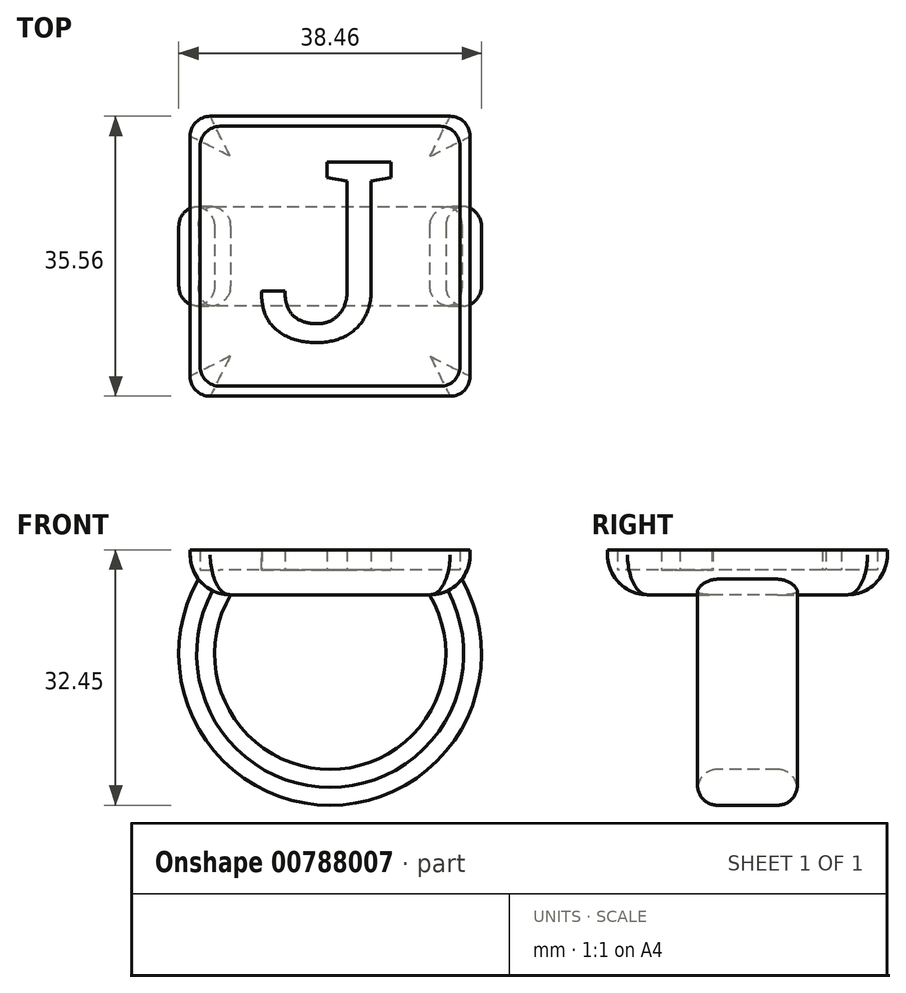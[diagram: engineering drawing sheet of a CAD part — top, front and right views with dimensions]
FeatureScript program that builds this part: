
annotation { "Feature Type Name" : "Feature", "Feature Type Description" : "" }
export const myFeature = defineFeature(function(context is Context, id is Id, definition is map)
    precondition{}
    {
        {
            var Q0;
            Q0=qCreatedBy(makeId("Top.planeOp"),FACE);
            var sketch = newSketch(context, id + "F0", { "sketchPlane" : qUnion([Q0])});
            skLineSegment(sketch, "E0.bottom", {"start": v(17.78, -17.78) * mm, "end": v(-17.78, -17.78) * mm});
            skLineSegment(sketch, "E0.top", {"start": v(17.78, 17.78) * mm, "end": v(-17.78, 17.78) * mm});
            skLineSegment(sketch, "E0.left", {"start": v(17.78, -17.78) * mm, "end": v(17.78, 17.78) * mm});
            skLineSegment(sketch, "E0.right", {"start": v(-17.78, -17.78) * mm, "end": v(-17.78, 17.78) * mm});
            skPoint(sketch, "E0.middle", {"position": v(0, 0) * mm});
            skSolve(sketch);
        }
        {
            var Q0;
            Q0 = qSketchRegion(id + "F0", true);
            extrude(context, id + "F1", {"entities" : qUnion([Q0]), "depth" : 3.17 * mm, "offsetDistance" : 25 * mm});
        }
        {
            var Q0;
            Q0=qCreatedBy(makeId("Front.planeOp"),FACE);
            var sketch = newSketch(context, id + "F2", { "sketchPlane" : qUnion([Q0])});
            skArc(sketch, "E1", {"start": v(-14.7, 0) * mm, "mid": v(0, -24.01) * mm, "end": v(14.7, 0) * mm});
            skSolve(sketch);
        }
        {
            var Q0;
            Q0=makeQuery(id+"F1.opExtrude","CAP_FACE",FACE,{"disambiguationData":[OSD([sQuery(id+"F0.wireOp",EDGE,"E0.bottom"),sQuery(id+"F0.wireOp",EDGE,"E0.top"),sQuery(id+"F0.wireOp",EDGE,"E0.left"),sQuery(id+"F0.wireOp",EDGE,"E0.right")])],"isStart":true});
            var sketch = newSketch(context, id + "F3", { "sketchPlane" : qUnion([Q0])});
            skLineSegment(sketch, "E2.bottom", {"start": v(-12.62, -6.35) * mm, "end": v(-17.7, -6.35) * mm});
            skLineSegment(sketch, "E2.top", {"start": v(-12.62, 6.35) * mm, "end": v(-17.7, 6.35) * mm});
            skLineSegment(sketch, "E2.left", {"start": v(-12.62, -6.35) * mm, "end": v(-12.62, 6.35) * mm});
            skLineSegment(sketch, "E2.right", {"start": v(-17.7, -6.35) * mm, "end": v(-17.7, 6.35) * mm});
            skPoint(sketch, "E2.middle", {"position": v(-15.16, 0) * mm});
            skSolve(sketch);
        }
        {
            var Q0;
            Q0=makeQuery(id+"F3.imprint","IMPRINT",FACE,{"disambiguationData":[TD([[makeQuery(id+"F3.imprint","IMPRINT",EDGE,{"derivedFrom":sQuery(id+"F3.wireOp",EDGE,"E2.bottom")}),-1.0]])]});
            var Q1;
            Q1 = qConstructionFilter(qBodyType(qCreatedBy(id + "F2" ,EDGE), BodyType.WIRE), ConstructionObject.NO);
            sweep(context, id + "F4", {"operationType" : NewBodyOperationType.ADD, "profiles" : qUnion([Q0]), "path" : qUnion([Q1])});
        }
        {
            var Q0;
            Q0=makeQuery(id+"F4.opSweep","SWEPT_FACE",FACE,{"disambiguationData":[OSD([sQuery(id+"F2.wireOp",EDGE,"E1"),sQuery(id+"F3.wireOp",EDGE,"E2.top")])]});
            var sketch = newSketch(context, id + "F5", { "sketchPlane" : qUnion([Q0])});
            skLineSegment(sketch, "E3.0", {"start": v(17.78, 0) * mm, "end": v(-17.78, 0) * mm});
            skArc(sketch, "E3.1", {"start": v(-12.62, 0) * mm, "mid": v(0, -22.19) * mm, "end": v(12.62, 0) * mm});
            skLineSegment(sketch, "E3.2", {"start": v(13.48, -1.69) * mm, "end": v(14.7, 0) * mm});
            skSolve(sketch);
        }
        {
            var Q0;
            {var subQ0=sQuery(id+"F5.wireOp",EDGE,"E3.2");Q0=makeQuery(id+"F5.imprint","IMPRINT",FACE,{"disambiguationData":[TD([[makeQuery(id+"F5.imprint","IMPRINT",EDGE,{"derivedFrom":subQ0}),1.0]])]});}
            var Q1;
            Q1=makeQuery(id+"F4.opSweep","SWEPT_FACE",FACE,{"disambiguationData":[OSD([sQuery(id+"F2.wireOp",EDGE,"E1"),sQuery(id+"F3.wireOp",EDGE,"E2.top")])]});
            var Q2;
            Q2=makeQuery(id+"F4.opSweep","SWEPT_FACE",FACE,{"disambiguationData":[OSD([sQuery(id+"F2.wireOp",EDGE,"E1"),sQuery(id+"F3.wireOp",EDGE,"E2.bottom")])]});
            extrude(context, id + "F6", {"entities" : qUnion([Q0]), "operationType" : NewBodyOperationType.ADD, "depth" : 0 * mm, "endBoundEntityFace" : qUnion([Q1]), "offsetDistance" : 25.4 * mm, "hasSecondDirection" : true, "secondDirectionBound" : SecondDirectionBoundingType.UP_TO_SURFACE, "secondDirectionOppositeDirection" : true, "secondDirectionDepth" : 25.4 * mm, "secondDirectionBoundEntityFace" : qUnion([Q2])});
        }
        {
            var Q0;
            Q0=makeQuery(id+"F6.boolean.opBoolean","MERGE",EDGE,{"derivedFrom":[makeQuery(id+"F4.opSweep","SWEPT_EDGE",EDGE,{"disambiguationData":[OSD([sQuery(id+"F2.wireOp",EDGE,"E1"),sQuery(id+"F3.wireOp",EDGE,"E2.top"),sQuery(id+"F3.wireOp",EDGE,"E2.left")])]}),makeQuery(id+"F6.opExtrude","CAP_EDGE",EDGE,{"disambiguationData":[OSD([sQuery(id+"F5.wireOp",EDGE,"E3.1")])],"isStart":false})]});
            var Q1;
            {var subQ0=sQuery(id+"F5.wireOp",EDGE,"E3.1");var subQ1=sQuery(id+"F3.wireOp",EDGE,"E2.bottom");var subQ2=sQuery(id+"F2.wireOp",EDGE,"E1");Q1=makeQuery(id+"F6.boolean.opBoolean","MERGE",EDGE,{"derivedFrom":[makeQuery(id+"F4.opSweep","SWEPT_EDGE",EDGE,{"disambiguationData":[OSD([subQ2,subQ1,sQuery(id+"F3.wireOp",EDGE,"E2.left")])]}),makeQuery(id+"F6.opExtrude","TWEAK_EDGE",EDGE,{"derivedFrom":[makeQuery(id+"F4.opSweep","SWEPT_FACE",FACE,{"disambiguationData":[OSD([subQ2,subQ1])]}),makeQuery(id+"F5.imprint","IMPRINT",EDGE,{"disambiguationData":[TD([[makeQuery(id+"F5.imprint","INTERSECT",VERTEX,{"derivedFrom":[subQ0,sQuery(id+"F5.wireOp",EDGE,"E3.2")]}),-1.0]])],"derivedFrom":subQ0})]})]});}
            var Q2;
            Q2=makeQuery(id+"F4.opSweep","SWEPT_EDGE",EDGE,{"disambiguationData":[OSD([sQuery(id+"F2.wireOp",EDGE,"E1"),sQuery(id+"F3.wireOp",EDGE,"E2.top"),sQuery(id+"F3.wireOp",EDGE,"E2.right")])]});
            var Q3;
            Q3=makeQuery(id+"F4.opSweep","SWEPT_EDGE",EDGE,{"disambiguationData":[OSD([sQuery(id+"F2.wireOp",EDGE,"E1"),sQuery(id+"F3.wireOp",EDGE,"E2.bottom"),sQuery(id+"F3.wireOp",EDGE,"E2.right")])]});
            fillet(context, id + "F7", {"entities" : qUnion([Q0, Q1, Q2, Q3]), "radius" : 2.54 * mm, "tangentPropagation" : true, "allowEdgeOverflow" : false});
        }
        {
            var Q0;
            Q0=makeQuery(id+"F1.opExtrude","CAP_FACE",FACE,{"disambiguationData":[OSD([sQuery(id+"F0.wireOp",EDGE,"E0.bottom"),sQuery(id+"F0.wireOp",EDGE,"E0.top"),sQuery(id+"F0.wireOp",EDGE,"E0.left"),sQuery(id+"F0.wireOp",EDGE,"E0.right")])],"isStart":false});
            var sketch = newSketch(context, id + "F8", { "sketchPlane" : qUnion([Q0])});
            skLineSegment(sketch, "E4.0", {"start": v(16.51, -13.97) * mm, "end": v(16.51, 13.97) * mm});
            skLineSegment(sketch, "E4.1", {"start": v(-13.97, -16.51) * mm, "end": v(13.97, -16.5) * mm});
            skLineSegment(sketch, "E4.2", {"start": v(-16.51, 13.97) * mm, "end": v(-16.51, -13.97) * mm});
            skLineSegment(sketch, "E4.3", {"start": v(13.97, 16.51) * mm, "end": v(-13.97, 16.5) * mm});
            skText(sketch, "E5", { "text": "J", "fontName": "RobotoSlab-Regular.ttf"});
            skPoint(sketch, "E6", {"position": v(-16.51, 0) * mm});
            skPoint(sketch, "E7.visualSharp", {"position": v(-16.51, 16.5) * mm});
            skArc(sketch, "E7.filletArc", {"start": v(-13.97, 16.5) * mm, "mid": v(-15.77, 15.77) * mm, "end": v(-16.51, 13.97) * mm});
            skPoint(sketch, "E8.visualSharp", {"position": v(-16.51, -16.51) * mm});
            skArc(sketch, "E8.filletArc", {"start": v(-16.5, -13.97) * mm, "mid": v(-15.77, -15.77) * mm, "end": v(-13.97, -16.51) * mm});
            skPoint(sketch, "E9.visualSharp", {"position": v(16.51, -16.5) * mm});
            skArc(sketch, "E9.filletArc", {"start": v(13.97, -16.51) * mm, "mid": v(15.77, -15.77) * mm, "end": v(16.51, -13.97) * mm});
            skPoint(sketch, "E10.visualSharp", {"position": v(16.5, 16.51) * mm});
            skArc(sketch, "E10.filletArc", {"start": v(16.5, 13.97) * mm, "mid": v(15.77, 15.77) * mm, "end": v(13.97, 16.51) * mm});
            const initialGuessF8  = {"E5": [-0.0097, -0.01063, 1, 0, 0.02286]};
            skSetInitialGuess(sketch, initialGuessF8);
            skSolve(sketch);
        }
        {
            var Q0;
            Q0=makeQuery(id+"F8.imprint","IMPRINT",FACE,{"disambiguationData":[TD([[makeQuery(id+"F8.imprint","IMPRINT",EDGE,{"derivedFrom":sQuery(id+"F8.wireOp",EDGE,"E5.sketch_text.stroke-0")}),-1.0]])]});
            var Q1;
            Q1=makeQuery(id+"F8.imprint","IMPRINT",FACE,{"disambiguationData":[TD([[makeQuery(id+"F8.imprint","IMPRINT",EDGE,{"derivedFrom":sQuery(id+"F8.wireOp",EDGE,"E4.0")}),-1.0]])]});
            extrude(context, id + "F9", {"entities" : qUnion([Q0, Q1]), "operationType" : NewBodyOperationType.ADD, "depth" : 2.54 * mm, "offsetDistance" : 25.4 * mm});
        }
        {
            var Q0;
            Q0=makeQuery(id+"F1.opExtrude","CAP_EDGE",EDGE,{"disambiguationData":[OSD([sQuery(id+"F0.wireOp",EDGE,"E0.bottom")])],"isStart":true});
            var Q1;
            Q1=makeQuery(id+"F1.opExtrude","CAP_EDGE",EDGE,{"disambiguationData":[OSD([sQuery(id+"F0.wireOp",EDGE,"E0.left")])],"isStart":true});
            var Q2;
            Q2=makeQuery(id+"F1.opExtrude","CAP_EDGE",EDGE,{"disambiguationData":[OSD([sQuery(id+"F0.wireOp",EDGE,"E0.top")])],"isStart":true});
            var Q3;
            Q3=makeQuery(id+"F1.opExtrude","CAP_EDGE",EDGE,{"disambiguationData":[OSD([sQuery(id+"F0.wireOp",EDGE,"E0.right")])],"isStart":true});
            fillet(context, id + "F10", {"entities" : qUnion([Q0, Q1, Q2, Q3]), "radius" : 5.08 * mm, "tangentPropagation" : true, "allowEdgeOverflow" : false});
        }
        {
            var Q0;
            Q0=makeQuery(id+"F10.opFillet","BLEND_EDGE",EDGE,{"blendedFrom":[makeQuery(id+"F1.opExtrude","CAP_EDGE",EDGE,{"disambiguationData":[OSD([sQuery(id+"F0.wireOp",EDGE,"E0.bottom")])],"isStart":true}),makeQuery(id+"F1.opExtrude","CAP_EDGE",EDGE,{"disambiguationData":[OSD([sQuery(id+"F0.wireOp",EDGE,"E0.left")])],"isStart":true})],"blendedInto":[]});
            var Q1;
            Q1=makeQuery(id+"F10.opFillet","BLEND_EDGE",EDGE,{"blendedFrom":[makeQuery(id+"F1.opExtrude","CAP_EDGE",EDGE,{"disambiguationData":[OSD([sQuery(id+"F0.wireOp",EDGE,"E0.top")])],"isStart":true}),makeQuery(id+"F1.opExtrude","CAP_EDGE",EDGE,{"disambiguationData":[OSD([sQuery(id+"F0.wireOp",EDGE,"E0.left")])],"isStart":true})],"blendedInto":[]});
            var Q2;
            Q2=makeQuery(id+"F10.opFillet","BLEND_EDGE",EDGE,{"blendedFrom":[makeQuery(id+"F1.opExtrude","CAP_EDGE",EDGE,{"disambiguationData":[OSD([sQuery(id+"F0.wireOp",EDGE,"E0.top")])],"isStart":true}),makeQuery(id+"F1.opExtrude","CAP_EDGE",EDGE,{"disambiguationData":[OSD([sQuery(id+"F0.wireOp",EDGE,"E0.right")])],"isStart":true})],"blendedInto":[]});
            var Q3;
            Q3=makeQuery(id+"F10.opFillet","BLEND_EDGE",EDGE,{"blendedFrom":[makeQuery(id+"F1.opExtrude","CAP_EDGE",EDGE,{"disambiguationData":[OSD([sQuery(id+"F0.wireOp",EDGE,"E0.bottom")])],"isStart":true}),makeQuery(id+"F1.opExtrude","CAP_EDGE",EDGE,{"disambiguationData":[OSD([sQuery(id+"F0.wireOp",EDGE,"E0.right")])],"isStart":true})],"blendedInto":[]});
            fillet(context, id + "F11", {"entities" : qUnion([Q0, Q1, Q2, Q3]), "radius" : 2.54 * mm, "tangentPropagation" : true, "allowEdgeOverflow" : false});
        }
    });
